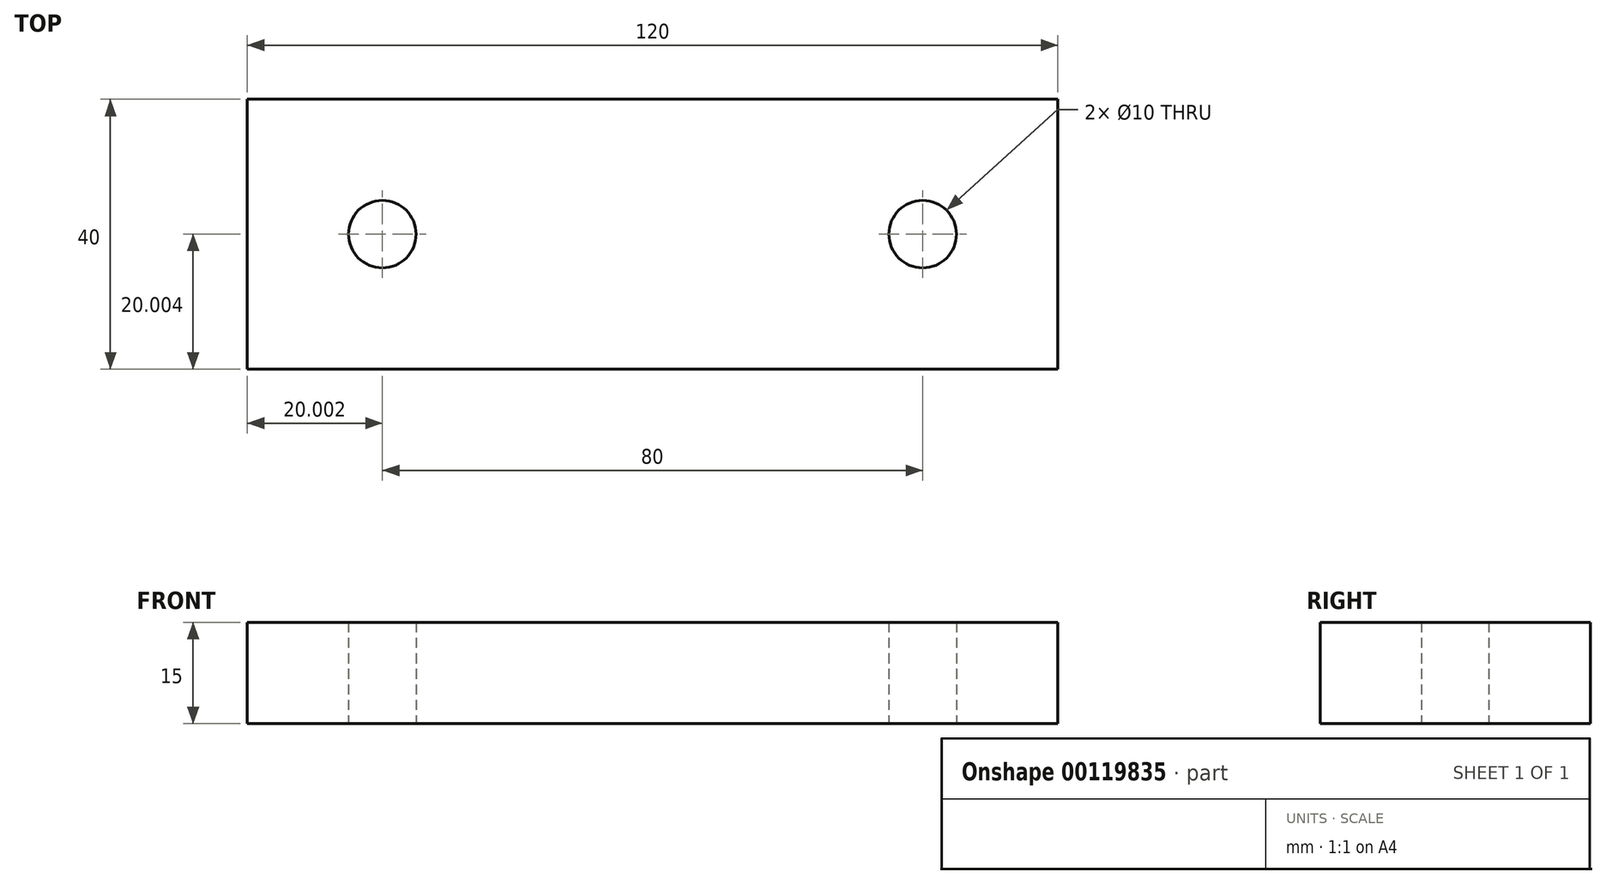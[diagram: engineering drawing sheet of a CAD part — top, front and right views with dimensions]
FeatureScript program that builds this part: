
annotation { "Feature Type Name" : "Feature", "Feature Type Description" : "" }
export const myFeature = defineFeature(function(context is Context, id is Id, definition is map)
    precondition{}
    {
        {
            var Q0;
            Q0=qCreatedBy(makeId("Top.planeOp"),FACE);
            var sketch = newSketch(context, id + "F0", { "sketchPlane" : qUnion([Q0])});
            skLineSegment(sketch, "E0.bottom", {"start": v(-46.56, 21.98) * mm, "end": v(73.44, 21.98) * mm});
            skLineSegment(sketch, "E0.top", {"start": v(-46.56, -18.02) * mm, "end": v(73.44, -18.02) * mm});
            skLineSegment(sketch, "E0.left", {"start": v(-46.56, 21.98) * mm, "end": v(-46.56, -18.02) * mm});
            skLineSegment(sketch, "E0.right", {"start": v(73.44, 21.98) * mm, "end": v(73.44, -18.02) * mm});
            skLineSegment(sketch, "E1", {"start": v(-46.56, 1.98) * mm, "end": v(73.44, 1.98) * mm, "construction": true});
            skCircle(sketch, "E2", {"center": v(-26.56, 1.98) * mm, "radius": 5 * mm});
            skCircle(sketch, "E3", {"center": v(53.44, 1.98) * mm, "radius": 5 * mm});
            skSolve(sketch);
        }
        {
            var Q0;
            Q0=makeQuery(id+"F0.imprint","IMPRINT",FACE,{"disambiguationData":[TD([[makeQuery(id+"F0.imprint","IMPRINT",EDGE,{"derivedFrom":sQuery(id+"F0.wireOp",EDGE,"E0.bottom")}),-1.0]])]});
            extrude(context, id + "F1", {"entities" : qUnion([Q0]), "depth" : 15 * mm});
        }
    });
